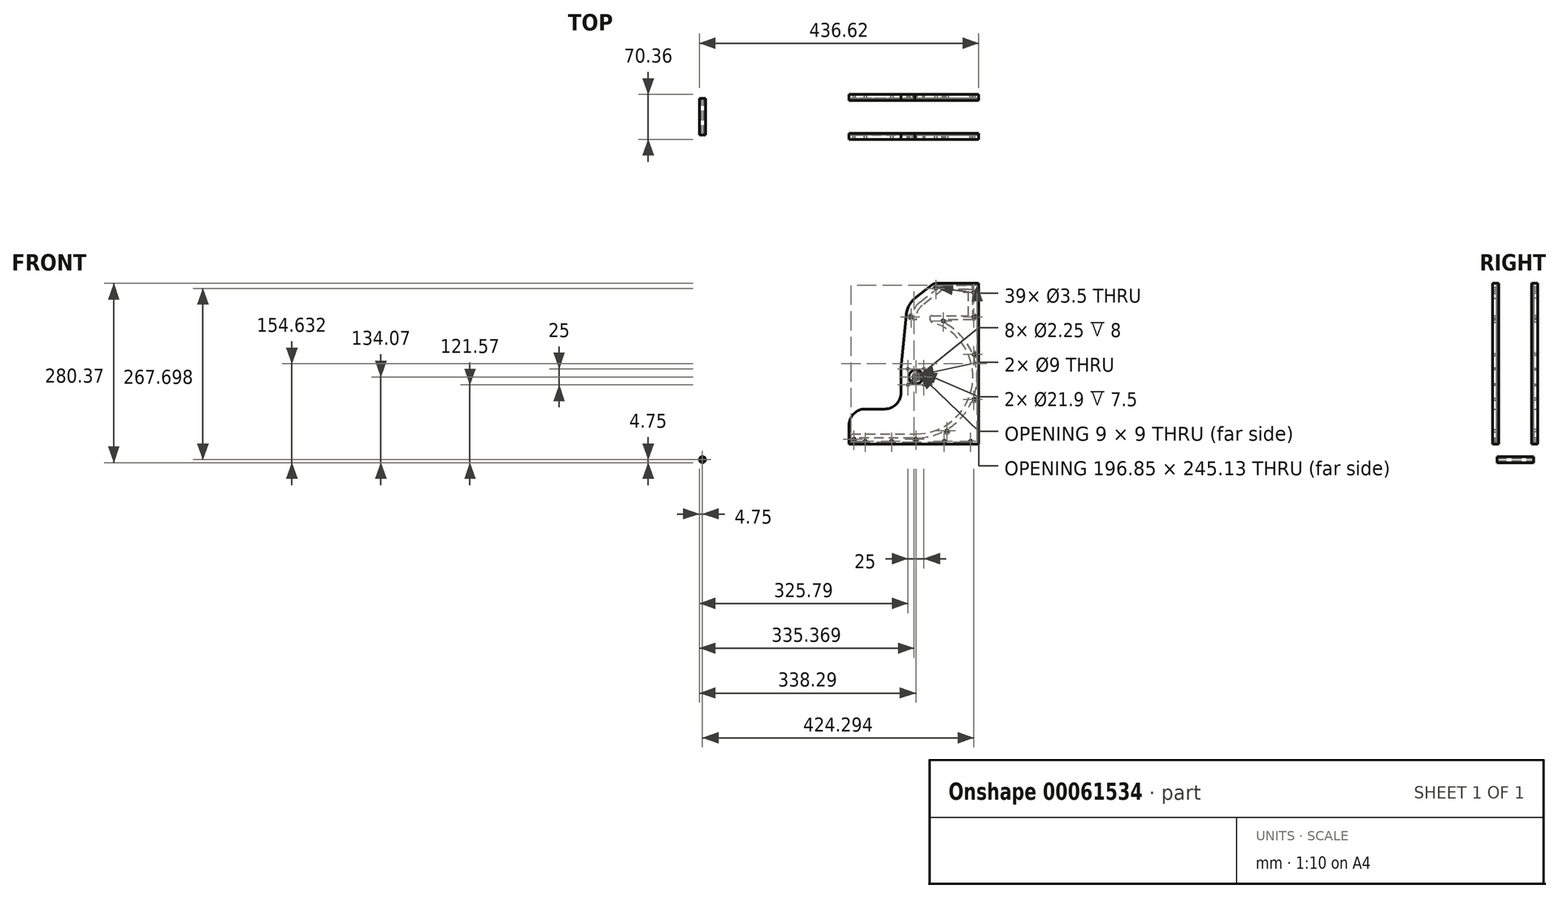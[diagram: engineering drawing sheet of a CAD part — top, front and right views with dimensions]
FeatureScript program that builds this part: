
annotation { "Feature Type Name" : "Feature", "Feature Type Description" : "" }
export const myFeature = defineFeature(function(context is Context, id is Id, definition is map)
    precondition{}
    {
        {
            var Q0;
            Q0=qCreatedBy(makeId("Front.planeOp"),FACE);
            var sketch = newSketch(context, id + "F0", { "sketchPlane" : qUnion([Q0])});
            skArc(sketch, "E0", {"start": v(0, -89.15) * mm, "mid": v(88.25, -12.66) * mm, "end": v(25.06, 85.56) * mm});
            skArc(sketch, "E1", {"start": v(4.37, -95.4) * mm, "mid": v(24.68, -92.26) * mm, "end": v(43.84, -84.85) * mm});
            skLineSegment(sketch, "E2.bottom", {"start": v(0, -89.15) * mm, "end": v(-101.35, -89.15) * mm});
            skLineSegment(sketch, "E2.top", {"start": v(-4.42, -95.5) * mm, "end": v(-92.18, -95.5) * mm});
            skLineSegment(sketch, "E2.right", {"start": v(-101.35, -89.15) * mm, "end": v(-101.35, -95.5) * mm});
            skLineSegment(sketch, "E3.bottom", {"start": v(82.3, 95.5) * mm, "end": v(24.82, 95.5) * mm});
            skLineSegment(sketch, "E4", {"start": v(22.07, 90.74) * mm, "end": v(25.06, 85.56) * mm});
            skLineSegment(sketch, "E5", {"start": v(95.5, -138.78) * mm, "end": v(95.5, 0) * mm, "construction": true});
            skCircle(sketch, "E6", {"center": v(42.65, 87.4) * mm, "radius": 1.75 * mm});
            skCircle(sketch, "E7", {"center": v(90.75, 34.96) * mm, "radius": 1.75 * mm});
            skArc(sketch, "E8", {"start": v(90.6, 30.21) * mm, "mid": v(95.19, 36.67) * mm, "end": v(87.45, 38.38) * mm});
            skCircle(sketch, "E9", {"center": v(90.75, -34.96) * mm, "radius": 1.75 * mm});
            skArc(sketch, "E10", {"start": v(87.45, -38.38) * mm, "mid": v(95.19, -36.67) * mm, "end": v(90.6, -30.21) * mm});
            skCircle(sketch, "E11", {"center": v(48.56, -84.27) * mm, "radius": 1.75 * mm});
            skArc(sketch, "E12", {"start": v(43.84, -84.85) * mm, "mid": v(50.93, -88.38) * mm, "end": v(51.42, -80.48) * mm});
            skCircle(sketch, "E13", {"center": v(-333.54, -129.32) * mm, "radius": 1.75 * mm});
            skCircle(sketch, "E14", {"center": v(-333.54, -129.32) * mm, "radius": 4.75 * mm});
            skCircle(sketch, "E15", {"center": v(-96.6, -97.25) * mm, "radius": 1.75 * mm});
            skArc(sketch, "E16", {"start": v(-101.01, -95.5) * mm, "mid": v(-96.6, -102) * mm, "end": v(-92.18, -95.5) * mm});
            skCircle(sketch, "E17", {"center": v(0, -97.25) * mm, "radius": 1.75 * mm});
            skArc(sketch, "E18", {"start": v(-4.42, -95.5) * mm, "mid": v(0.05, -102) * mm, "end": v(4.37, -95.4) * mm});
            skLineSegment(sketch, "E19.trimOffspring", {"start": v(-101.01, -95.5) * mm, "end": v(-101.35, -95.5) * mm});
            skArc(sketch, "E20.trimOffspring", {"start": v(51.42, -80.48) * mm, "mid": v(72.56, -62.1) * mm, "end": v(87.45, -38.38) * mm});
            skArc(sketch, "E21.trimOffspring", {"start": v(90.6, -30.21) * mm, "mid": v(95.5, 0) * mm, "end": v(90.6, 30.21) * mm});
            skArc(sketch, "E22.trimOffspring", {"start": v(87.45, 38.38) * mm, "mid": v(70.38, 64.56) * mm, "end": v(45.77, 83.82) * mm});
            skArc(sketch, "E23.trimOffspring", {"start": v(45.77, 83.82) * mm, "mid": v(47.26, 86.28) * mm, "end": v(47.06, 89.15) * mm});
            skLineSegment(sketch, "E24.trimOffspring", {"start": v(88.66, 89.15) * mm, "end": v(47.06, 89.15) * mm});
            skCircle(sketch, "E25", {"center": v(90.4, 93.9) * mm, "radius": 1.75 * mm});
            skArc(sketch, "E26", {"start": v(88.66, 89.49) * mm, "mid": v(95.16, 93.9) * mm, "end": v(88.66, 98.32) * mm});
            skLineSegment(sketch, "E27", {"start": v(88.66, 136.78) * mm, "end": v(88.66, 136.44) * mm});
            skLineSegment(sketch, "E28", {"start": v(82.3, 136.78) * mm, "end": v(82.3, 95.5) * mm});
            skLineSegment(sketch, "E29", {"start": v(82.3, 136.78) * mm, "end": v(88.66, 136.78) * mm});
            skLineSegment(sketch, "E30.trimOffspring", {"start": v(88.66, 89.49) * mm, "end": v(88.66, 89.15) * mm});
            skCircle(sketch, "E31", {"center": v(90.4, 132.03) * mm, "radius": 1.75 * mm});
            skArc(sketch, "E32", {"start": v(88.66, 127.61) * mm, "mid": v(95.16, 132.03) * mm, "end": v(88.66, 136.44) * mm});
            skLineSegment(sketch, "E33.trimOffspring", {"start": v(88.66, 127.61) * mm, "end": v(88.66, 98.32) * mm});
            skPoint(sketch, "E34.visualSharp", {"position": v(19.32, 95.5) * mm});
            skArc(sketch, "E34.filletArc", {"start": v(24.82, 95.5) * mm, "mid": v(22.07, 93.92) * mm, "end": v(22.07, 90.74) * mm});
            skSolve(sketch);
        }
        {
            var Q0;
            Q0=qSketchRegion(id+"F0",true);
            extrude(context, id + "F1", {"entities" : qUnion([Q0]), "depth" : 57.15 * mm});
        }
        {
            var Q0;
            Q0=qCreatedBy(makeId("Front.planeOp"),FACE);
            var sketch = newSketch(context, id + "F2", { "sketchPlane" : qUnion([Q0])});
            skArc(sketch, "E35", {"start": v(0.64, 89.15) * mm, "mid": v(-2.36, 89.12) * mm, "end": v(-5.35, 89) * mm});
            skLineSegment(sketch, "E36", {"start": v(0, 0) * mm, "end": v(0, 123.17) * mm, "construction": true});
            skLineSegment(sketch, "E37", {"start": v(119.91, 115.4) * mm, "end": v(119.91, 121.76) * mm});
            skLineSegment(sketch, "E38.0", {"start": v(82.3, 95.5) * mm, "end": v(24.82, 95.5) * mm, "construction": true});
            skArc(sketch, "E39.0", {"start": v(24.82, 95.5) * mm, "mid": v(22.07, 93.92) * mm, "end": v(22.07, 90.74) * mm, "construction": true});
            skArc(sketch, "E40", {"start": v(9.89, 111.61) * mm, "mid": v(2.27, 101.61) * mm, "end": v(0.64, 89.15) * mm});
            skCircle(sketch, "E41", {"center": v(-7.26, 93.62) * mm, "radius": 1.75 * mm});
            skArc(sketch, "E42", {"start": v(-5.15, 97.88) * mm, "mid": v(-12.01, 93.75) * mm, "end": v(-5.38, 89.26) * mm});
            skArc(sketch, "E43.trimOffspring", {"start": v(6.19, 116.77) * mm, "mid": v(-1.26, 108.4) * mm, "end": v(-5.15, 97.88) * mm});
            skArc(sketch, "E44.trimOffspring", {"start": v(-5.38, 89.26) * mm, "mid": v(-5.34, 88.91) * mm, "end": v(-5.3, 88.57) * mm});
            skLineSegment(sketch, "E45", {"start": v(88.66, 136.78) * mm, "end": v(88.66, 143.13) * mm});
            skLineSegment(sketch, "E46", {"start": v(88.66, 143.13) * mm, "end": v(40.23, 143.13) * mm});
            skPoint(sketch, "E47.0.start.orphan", {"position": v(82.3, 136.78) * mm});
            skLineSegment(sketch, "E48", {"start": v(88.66, 136.78) * mm, "end": v(42.4, 136.78) * mm});
            skLineSegment(sketch, "E49", {"start": v(6.19, 116.77) * mm, "end": v(28.82, 134.3) * mm});
            skLineSegment(sketch, "E50.0", {"start": v(9.89, 111.61) * mm, "end": v(42.4, 136.78) * mm});
            skPoint(sketch, "E51.orphan", {"position": v(32.03, 136.78) * mm});
            skPoint(sketch, "E52.orphan", {"position": v(-24.6, 136.78) * mm});
            skCircle(sketch, "E53", {"center": v(31.24, 138.38) * mm, "radius": 1.75 * mm});
            skArc(sketch, "E54", {"start": v(35.8, 139.7) * mm, "mid": v(28.33, 142.14) * mm, "end": v(28.82, 134.3) * mm});
            skLineSegment(sketch, "E55.trimOffspring", {"start": v(35.8, 139.7) * mm, "end": v(40.23, 143.13) * mm});
            skLineSegment(sketch, "E56.trimOffspring", {"start": v(32.03, 136.78) * mm, "end": v(32.3, 137) * mm});
            skSolve(sketch);
        }
        {
            var Q0;
            Q0=qSketchRegion(id+"F2",true);
            var Q1;
            Q1=makeQuery(id+"F1.opExtrude","CAP_FACE",FACE,{"disambiguationData":[OSD([sQuery(id+"F0.wireOp",EDGE,"E0"),sQuery(id+"F0.wireOp",EDGE,"E1"),sQuery(id+"F0.wireOp",EDGE,"E2.bottom"),sQuery(id+"F0.wireOp",EDGE,"E2.top"),sQuery(id+"F0.wireOp",EDGE,"E2.right"),sQuery(id+"F0.wireOp",EDGE,"E3.bottom"),sQuery(id+"F0.wireOp",EDGE,"E4"),sQuery(id+"F0.wireOp",EDGE,"E6"),sQuery(id+"F0.wireOp",EDGE,"E7"),sQuery(id+"F0.wireOp",EDGE,"E8"),sQuery(id+"F0.wireOp",EDGE,"E9"),sQuery(id+"F0.wireOp",EDGE,"E10"),sQuery(id+"F0.wireOp",EDGE,"E11"),sQuery(id+"F0.wireOp",EDGE,"E12"),sQuery(id+"F0.wireOp",EDGE,"E15"),sQuery(id+"F0.wireOp",EDGE,"E16"),sQuery(id+"F0.wireOp",EDGE,"E17"),sQuery(id+"F0.wireOp",EDGE,"E18"),sQuery(id+"F0.wireOp",EDGE,"E19.trimOffspring"),sQuery(id+"F0.wireOp",EDGE,"E20.trimOffspring"),sQuery(id+"F0.wireOp",EDGE,"E21.trimOffspring"),sQuery(id+"F0.wireOp",EDGE,"E22.trimOffspring"),sQuery(id+"F0.wireOp",EDGE,"E23.trimOffspring"),sQuery(id+"F0.wireOp",EDGE,"E24.trimOffspring"),sQuery(id+"F0.wireOp",EDGE,"E25"),sQuery(id+"F0.wireOp",EDGE,"E26"),sQuery(id+"F0.wireOp",EDGE,"E27"),sQuery(id+"F0.wireOp",EDGE,"E28"),sQuery(id+"F0.wireOp",EDGE,"E29"),sQuery(id+"F0.wireOp",EDGE,"E30.trimOffspring"),sQuery(id+"F0.wireOp",EDGE,"E31"),sQuery(id+"F0.wireOp",EDGE,"E32"),sQuery(id+"F0.wireOp",EDGE,"E33.trimOffspring"),sQuery(id+"F0.wireOp",EDGE,"E34.filletArc")])],"isStart":false});
            extrude(context, id + "F3", {"entities" : qUnion([Q0]), "endBound" : BoundingType.UP_TO_SURFACE, "endBoundEntityFace" : qUnion([Q1]), "depth" : 25.4 * mm});
        }
        {
            var Q0;
            Q0=qCreatedBy(makeId("Front.planeOp"),FACE);
            var sketch = newSketch(context, id + "F4", { "sketchPlane" : qUnion([Q0])});
            skLineSegment(sketch, "E57.bottom", {"start": v(98.33, 146.3) * mm, "end": v(-104.52, 146.3) * mm});
            skLineSegment(sketch, "E57.top", {"start": v(98.33, -105.18) * mm, "end": v(-104.52, -105.18) * mm});
            skLineSegment(sketch, "E57.left", {"start": v(98.33, 146.3) * mm, "end": v(98.33, -105.18) * mm});
            skLineSegment(sketch, "E57.right", {"start": v(-104.52, 146.3) * mm, "end": v(-104.52, -105.18) * mm});
            skSolve(sketch);
        }
        {
            var Q0;
            Q0=makeQuery(id+"F4.imprint","IMPRINT",FACE,{"disambiguationData":[TD([[makeQuery(id+"F4.imprint","IMPRINT",EDGE,{"derivedFrom":sQuery(id+"F4.wireOp",EDGE,"E57.bottom")}),1.0]])]});
            extrude(context, id + "F5", {"entities" : qUnion([Q0]), "depth" : 3.17 * mm, "hasSecondDirection" : true, "secondDirectionOppositeDirection" : true, "secondDirectionDepth" : 6.35 * mm});
        }
        {
            var Q0;
            Q0=makeQuery(id+"F5.opExtrude","CAP_FACE",FACE,{"disambiguationData":[OSD([sQuery(id+"F4.wireOp",EDGE,"E57.bottom"),sQuery(id+"F4.wireOp",EDGE,"E57.top"),sQuery(id+"F4.wireOp",EDGE,"E57.left"),sQuery(id+"F4.wireOp",EDGE,"E57.right")])],"isStart":true});
            var sketch = newSketch(context, id + "F6", { "sketchPlane" : qUnion([Q0])});
            skCircle(sketch, "E58", {"center": v(0, 0) * mm, "radius": 4.5 * mm});
            skSolve(sketch);
        }
        {
            var Q0;
            Q0 = qSketchRegion(id + "F6", true);
            extrude(context, id + "F7", {"entities" : qUnion([Q0]), "operationType" : NewBodyOperationType.REMOVE, "oppositeDirection" : true, "depth" : 25.4 * mm});
        }
        {
            var Q0;
            Q0=makeQuery(id+"F5.opExtrude","CAP_FACE",FACE,{"disambiguationData":[OSD([sQuery(id+"F4.wireOp",EDGE,"E57.bottom"),sQuery(id+"F4.wireOp",EDGE,"E57.top"),sQuery(id+"F4.wireOp",EDGE,"E57.left"),sQuery(id+"F4.wireOp",EDGE,"E57.right")])],"isStart":true});
            var sketch = newSketch(context, id + "F8", { "sketchPlane" : qUnion([Q0])});
            skCircle(sketch, "E59", {"center": v(0, 0) * mm, "radius": 10.95 * mm});
            skSolve(sketch);
        }
        {
            var Q0;
            Q0 = qSketchRegion(id + "F8", true);
            extrude(context, id + "F9", {"entities" : qUnion([Q0]), "operationType" : NewBodyOperationType.REMOVE, "oppositeDirection" : true, "depth" : 7.5 * mm});
        }
        {
            var Q0;
            Q0=makeQuery(id+"F5.opExtrude","CAP_FACE",FACE,{"disambiguationData":[OSD([sQuery(id+"F4.wireOp",EDGE,"E57.bottom"),sQuery(id+"F4.wireOp",EDGE,"E57.top"),sQuery(id+"F4.wireOp",EDGE,"E57.left"),sQuery(id+"F4.wireOp",EDGE,"E57.right")])],"isStart":true});
            var sketch = newSketch(context, id + "F10", { "sketchPlane" : qUnion([Q0])});
            skLineSegment(sketch, "E60.bottom", {"start": v(-12.5, 12.5) * mm, "end": v(12.5, 12.5) * mm, "construction": true});
            skLineSegment(sketch, "E60.top", {"start": v(-12.5, -12.5) * mm, "end": v(12.5, -12.5) * mm, "construction": true});
            skLineSegment(sketch, "E60.left", {"start": v(-12.5, 12.5) * mm, "end": v(-12.5, -12.5) * mm, "construction": true});
            skLineSegment(sketch, "E60.right", {"start": v(12.5, 12.5) * mm, "end": v(12.5, -12.5) * mm, "construction": true});
            skCircle(sketch, "E61", {"center": v(12.5, -12.5) * mm, "radius": 1.13 * mm});
            skCircle(sketch, "E62", {"center": v(-12.5, -12.5) * mm, "radius": 1.13 * mm});
            skCircle(sketch, "E63", {"center": v(-12.5, 12.5) * mm, "radius": 1.13 * mm});
            skCircle(sketch, "E64", {"center": v(12.5, 12.5) * mm, "radius": 1.13 * mm});
            skSolve(sketch);
        }
        {
            var Q0;
            Q0 = qSketchRegion(id + "F10", true);
            extrude(context, id + "F11", {"entities" : qUnion([Q0]), "operationType" : NewBodyOperationType.REMOVE, "oppositeDirection" : true, "depth" : 8 * mm});
        }
        {
            var Q0;
            Q0=makeQuery(id+"F5.opExtrude","CAP_FACE",FACE,{"disambiguationData":[OSD([sQuery(id+"F4.wireOp",EDGE,"E57.bottom"),sQuery(id+"F4.wireOp",EDGE,"E57.top"),sQuery(id+"F4.wireOp",EDGE,"E57.left"),sQuery(id+"F4.wireOp",EDGE,"E57.right")])],"isStart":false});
            var sketch = newSketch(context, id + "F12", { "sketchPlane" : qUnion([Q0])});
            skLineSegment(sketch, "E65", {"start": v(-23.15, 13) * mm, "end": v(-23.15, -24.84) * mm});
            skLineSegment(sketch, "E66", {"start": v(-148.38, -50.24) * mm, "end": v(-48.55, -50.24) * mm});
            skArc(sketch, "E67.0.0", {"start": v(-5.15, 97.88) * mm, "mid": v(-1.26, 108.4) * mm, "end": v(6.19, 116.77) * mm, "construction": true});
            skArc(sketch, "E67.0.2", {"start": v(6.19, 116.77) * mm, "mid": v(-1.26, 108.4) * mm, "end": v(-5.15, 97.88) * mm, "construction": true});
            skArc(sketch, "E68.0", {"start": v(-1.75, 122.87) * mm, "mid": v(-10.96, 111) * mm, "end": v(-15.16, 96.59) * mm});
            skCircle(sketch, "E69.0", {"center": v(-12.5, 12.5) * mm, "radius": 1.13 * mm, "construction": true});
            skArc(sketch, "E70.0", {"start": v(-23.1, 13.51) * mm, "mid": v(-23.14, 13) * mm, "end": v(-23.15, 12.5) * mm});
            skLineSegment(sketch, "E71", {"start": v(-15.16, 96.59) * mm, "end": v(-23.15, 13) * mm});
            skLineSegment(sketch, "E72.trimOffspring", {"start": v(-1.75, 122.87) * mm, "end": v(42.2, 156.9) * mm});
            skPoint(sketch, "E73.visualSharp", {"position": v(-23.15, -50.24) * mm});
            skArc(sketch, "E73.filletArc", {"start": v(-48.55, -50.24) * mm, "mid": v(-30.59, -42.8) * mm, "end": v(-23.15, -24.84) * mm});
            skLineSegment(sketch, "E74", {"start": v(42.2, 156.9) * mm, "end": v(-148.38, 156.9) * mm});
            skLineSegment(sketch, "E75", {"start": v(-148.38, -50.24) * mm, "end": v(-148.38, 156.9) * mm});
            skSolve(sketch);
        }
        {
            var Q0;
            Q0 = qSketchRegion(id + "F12", true);
            extrude(context, id + "F13", {"entities" : qUnion([Q0]), "operationType" : NewBodyOperationType.REMOVE, "oppositeDirection" : true, "depth" : 25.4 * mm});
        }
        {
            var Q0;
            Q0=makeQuery(id+"F13.boolean.opBoolean","INTERSECT",EDGE,{"derivedFrom":[makeQuery(id+"F5.opExtrude","SWEPT_FACE",FACE,{"disambiguationData":[OSD([sQuery(id+"F4.wireOp",EDGE,"E57.bottom")])]}),makeQuery(id+"F13.opExtrude","SWEPT_FACE",FACE,{"disambiguationData":[OSD([sQuery(id+"F12.wireOp",EDGE,"E72.trimOffspring")])]})]});
            fillet(context, id + "F14", {"entities" : qUnion([Q0]), "radius" : 12.7 * mm, "tangentPropagation" : true, "allowEdgeOverflow" : false});
        }
        {
            var Q0;
            Q0=makeQuery(id+"F13.boolean.opBoolean","INTERSECT",EDGE,{"derivedFrom":[makeQuery(id+"F5.opExtrude","SWEPT_FACE",FACE,{"disambiguationData":[OSD([sQuery(id+"F4.wireOp",EDGE,"E57.right")])]}),makeQuery(id+"F13.opExtrude","SWEPT_FACE",FACE,{"disambiguationData":[OSD([sQuery(id+"F12.wireOp",EDGE,"E66")])]})]});
            fillet(context, id + "F15", {"entities" : qUnion([Q0]), "radius" : 25.4 * mm, "tangentPropagation" : true, "allowEdgeOverflow" : false});
        }
        {
            var Q0;
            Q0=makeQuery(id+"F5.opExtrude","CAP_FACE",FACE,{"disambiguationData":[OSD([sQuery(id+"F4.wireOp",EDGE,"E57.bottom"),sQuery(id+"F4.wireOp",EDGE,"E57.top"),sQuery(id+"F4.wireOp",EDGE,"E57.left"),sQuery(id+"F4.wireOp",EDGE,"E57.right")])],"isStart":false});
            var sketch = newSketch(context, id + "F16", { "sketchPlane" : qUnion([Q0])});
            skCircle(sketch, "E76.0", {"center": v(-96.6, -97.25) * mm, "radius": 1.75 * mm});
            skCircle(sketch, "E77.0", {"center": v(0, -97.25) * mm, "radius": 1.75 * mm});
            skCircle(sketch, "E78.0", {"center": v(48.56, -84.27) * mm, "radius": 1.75 * mm});
            skCircle(sketch, "E79.0", {"center": v(90.75, -34.96) * mm, "radius": 1.75 * mm});
            skCircle(sketch, "E80.0", {"center": v(90.75, 34.96) * mm, "radius": 1.75 * mm});
            skCircle(sketch, "E81.0", {"center": v(42.65, 87.4) * mm, "radius": 1.75 * mm});
            skCircle(sketch, "E82.0", {"center": v(90.4, 93.9) * mm, "radius": 1.75 * mm});
            skCircle(sketch, "E83.0", {"center": v(90.4, 132.03) * mm, "radius": 1.75 * mm});
            skCircle(sketch, "E84.0", {"center": v(31.24, 138.38) * mm, "radius": 1.75 * mm});
            skCircle(sketch, "E85.0", {"center": v(-7.26, 93.62) * mm, "radius": 1.75 * mm});
            skSolve(sketch);
        }
        {
            var Q0;
            Q0 = qSketchRegion(id + "F16", true);
            extrude(context, id + "F17", {"entities" : qUnion([Q0]), "operationType" : NewBodyOperationType.REMOVE, "oppositeDirection" : true, "depth" : 25.4 * mm});
        }
        {
            var Q0;
            Q0=makeQuery(id+"F5.opExtrude","CAP_FACE",FACE,{"disambiguationData":[OSD([sQuery(id+"F4.wireOp",EDGE,"E57.bottom"),sQuery(id+"F4.wireOp",EDGE,"E57.top"),sQuery(id+"F4.wireOp",EDGE,"E57.left"),sQuery(id+"F4.wireOp",EDGE,"E57.right")])],"isStart":false});
            var sketch = newSketch(context, id + "F18", { "sketchPlane" : qUnion([Q0])});
            skArc(sketch, "E86.0.0", {"start": v(25.06, 85.56) * mm, "mid": v(88.25, -12.66) * mm, "end": v(0, -89.15) * mm});
            skLineSegment(sketch, "E86.0.1", {"start": v(0, -89.15) * mm, "end": v(-101.35, -89.15) * mm});
            skLineSegment(sketch, "E86.0.2", {"start": v(-101.35, -89.15) * mm, "end": v(-101.35, -95.5) * mm});
            skLineSegment(sketch, "E86.0.3", {"start": v(-101.35, -95.5) * mm, "end": v(-101.01, -95.5) * mm});
            skArc(sketch, "E86.0.4", {"start": v(-101.01, -95.5) * mm, "mid": v(-96.6, -102) * mm, "end": v(-92.18, -95.5) * mm});
            skLineSegment(sketch, "E86.0.5", {"start": v(-92.18, -95.5) * mm, "end": v(-4.42, -95.5) * mm});
            skArc(sketch, "E86.0.6", {"start": v(-4.42, -95.5) * mm, "mid": v(0.05, -102) * mm, "end": v(4.37, -95.4) * mm});
            skArc(sketch, "E86.0.7", {"start": v(4.37, -95.4) * mm, "mid": v(24.68, -92.26) * mm, "end": v(43.84, -84.85) * mm});
            skArc(sketch, "E86.0.8", {"start": v(43.84, -84.85) * mm, "mid": v(50.93, -88.38) * mm, "end": v(51.42, -80.48) * mm});
            skArc(sketch, "E86.0.9", {"start": v(51.42, -80.48) * mm, "mid": v(72.56, -62.1) * mm, "end": v(87.45, -38.38) * mm});
            skArc(sketch, "E86.0.10", {"start": v(87.45, -38.38) * mm, "mid": v(95.19, -36.67) * mm, "end": v(90.6, -30.21) * mm});
            skArc(sketch, "E86.0.11", {"start": v(90.6, -30.21) * mm, "mid": v(95.5, 0) * mm, "end": v(90.6, 30.21) * mm});
            skArc(sketch, "E86.0.12", {"start": v(90.6, 30.21) * mm, "mid": v(95.19, 36.67) * mm, "end": v(87.45, 38.38) * mm});
            skArc(sketch, "E86.0.13", {"start": v(87.45, 38.38) * mm, "mid": v(70.38, 64.56) * mm, "end": v(45.77, 83.82) * mm});
            skArc(sketch, "E86.0.14", {"start": v(45.77, 83.82) * mm, "mid": v(47.26, 86.28) * mm, "end": v(47.06, 89.15) * mm});
            skLineSegment(sketch, "E86.0.15", {"start": v(47.06, 89.15) * mm, "end": v(88.66, 89.15) * mm});
            skLineSegment(sketch, "E86.0.16", {"start": v(88.66, 89.15) * mm, "end": v(88.66, 89.49) * mm});
            skArc(sketch, "E86.0.17", {"start": v(88.66, 89.49) * mm, "mid": v(95.16, 93.9) * mm, "end": v(88.66, 98.32) * mm});
            skLineSegment(sketch, "E86.0.18", {"start": v(88.66, 98.32) * mm, "end": v(88.66, 127.61) * mm});
            skArc(sketch, "E86.0.19", {"start": v(88.66, 127.61) * mm, "mid": v(95.16, 132.03) * mm, "end": v(88.66, 136.44) * mm});
            skLineSegment(sketch, "E86.0.20", {"start": v(88.66, 136.44) * mm, "end": v(88.66, 136.78) * mm});
            skLineSegment(sketch, "E86.0.21", {"start": v(88.66, 136.78) * mm, "end": v(82.3, 136.78) * mm});
            skLineSegment(sketch, "E86.0.22", {"start": v(82.3, 136.78) * mm, "end": v(82.3, 95.5) * mm});
            skLineSegment(sketch, "E86.0.23", {"start": v(82.3, 95.5) * mm, "end": v(24.82, 95.5) * mm});
            skArc(sketch, "E86.0.24", {"start": v(24.82, 95.5) * mm, "mid": v(22.07, 93.92) * mm, "end": v(22.07, 90.74) * mm});
            skLineSegment(sketch, "E86.0.25", {"start": v(22.07, 90.74) * mm, "end": v(25.06, 85.56) * mm});
            skArc(sketch, "E87.0.0", {"start": v(-5.35, 89) * mm, "mid": v(-2.36, 89.12) * mm, "end": v(0.64, 89.15) * mm});
            skArc(sketch, "E87.0.1", {"start": v(0.64, 89.15) * mm, "mid": v(2.27, 101.61) * mm, "end": v(9.89, 111.61) * mm});
            skLineSegment(sketch, "E87.0.2", {"start": v(9.89, 111.61) * mm, "end": v(42.4, 136.78) * mm});
            skLineSegment(sketch, "E87.0.3", {"start": v(42.4, 136.78) * mm, "end": v(88.66, 136.78) * mm});
            skLineSegment(sketch, "E87.0.4", {"start": v(88.66, 136.78) * mm, "end": v(88.66, 143.13) * mm});
            skLineSegment(sketch, "E87.0.5", {"start": v(88.66, 143.13) * mm, "end": v(40.23, 143.13) * mm});
            skLineSegment(sketch, "E87.0.6", {"start": v(40.23, 143.13) * mm, "end": v(35.8, 139.7) * mm});
            skArc(sketch, "E87.0.7", {"start": v(35.8, 139.7) * mm, "mid": v(28.33, 142.14) * mm, "end": v(28.82, 134.3) * mm});
            skLineSegment(sketch, "E87.0.8", {"start": v(28.82, 134.3) * mm, "end": v(6.19, 116.77) * mm});
            skArc(sketch, "E87.0.9", {"start": v(6.19, 116.77) * mm, "mid": v(-1.26, 108.4) * mm, "end": v(-5.15, 97.88) * mm});
            skArc(sketch, "E87.0.10", {"start": v(-5.15, 97.88) * mm, "mid": v(-12.01, 93.75) * mm, "end": v(-5.38, 89.26) * mm});
            skArc(sketch, "E87.0.11", {"start": v(-5.38, 89.26) * mm, "mid": v(-5.37, 89.13) * mm, "end": v(-5.35, 89) * mm});
            skSolve(sketch);
        }
        {
            var Q0;
            Q0 = qSketchRegion(id + "F18", true);
            extrude(context, id + "F19", {"entities" : qUnion([Q0]), "operationType" : NewBodyOperationType.REMOVE, "depth" : 63.5 * mm, "hasSecondDirection" : true, "secondDirectionOppositeDirection" : true, "secondDirectionDepth" : 2.92 * mm});
        }
        {
            var Q0;
            Q0=makeQuery(id+"F5.opExtrude","CAP_FACE",FACE,{"disambiguationData":[OSD([sQuery(id+"F4.wireOp",EDGE,"E57.bottom"),sQuery(id+"F4.wireOp",EDGE,"E57.top"),sQuery(id+"F4.wireOp",EDGE,"E57.left"),sQuery(id+"F4.wireOp",EDGE,"E57.right")])],"isStart":false});
            cPlane(context, id + "F20", {"entities" : qUnion([Q0]), "cplaneType" : CPlaneType.OFFSET, "offset" : 25.65 * mm, "width" : 152.4 * mm, "height" : 152.4 * mm});
        }
        {
            var Q0;
            Q0=makeQuery(id+"F5.opExtrude","SWEPT_BODY",BODY,{"disambiguationData":[OSD([sQuery(id+"F4.wireOp",EDGE,"E57.bottom"),sQuery(id+"F4.wireOp",EDGE,"E57.top"),sQuery(id+"F4.wireOp",EDGE,"E57.left"),sQuery(id+"F4.wireOp",EDGE,"E57.right")])]});
            var Q1;
            Q1=qCreatedBy(id+"F20.planeOp",FACE);
            mirror(context, id + "F21", {"entities" : qUnion([Q0]), "mirrorPlane" : qUnion([Q1])});
        }
        {
            var Q0;
            Q0=makeQuery(id+"F21.opPattern","COPY",FACE,{"derivedFrom":makeQuery(id+"F5.opExtrude","CAP_FACE",FACE,{"disambiguationData":[OSD([sQuery(id+"F4.wireOp",EDGE,"E57.bottom"),sQuery(id+"F4.wireOp",EDGE,"E57.top"),sQuery(id+"F4.wireOp",EDGE,"E57.left"),sQuery(id+"F4.wireOp",EDGE,"E57.right")])],"isStart":true}),"instanceName":"1"});
            var sketch = newSketch(context, id + "F22", { "sketchPlane" : qUnion([Q0])});
            skCircle(sketch, "E88", {"center": v(85.63, -100.42) * mm, "radius": 1.75 * mm});
            skCircle(sketch, "E89", {"center": v(44.36, -100.42) * mm, "radius": 1.75 * mm});
            skCircle(sketch, "E90", {"center": v(-79.12, -100.42) * mm, "radius": 1.75 * mm});
            skCircle(sketch, "E91", {"center": v(-37.85, -100.42) * mm, "radius": 1.75 * mm});
            skSolve(sketch);
        }
        {
            var Q0;
            Q0 = qSketchRegion(id + "F22", true);
            extrude(context, id + "F23", {"entities" : qUnion([Q0]), "operationType" : NewBodyOperationType.REMOVE, "endBound" : BoundingType.THROUGH_ALL, "oppositeDirection" : true, "depth" : 25.4 * mm});
        }
        {
            var Q0;
            Q0=makeQuery(id+"F5.opExtrude","CAP_FACE",FACE,{"disambiguationData":[OSD([sQuery(id+"F4.wireOp",EDGE,"E57.bottom"),sQuery(id+"F4.wireOp",EDGE,"E57.top"),sQuery(id+"F4.wireOp",EDGE,"E57.left"),sQuery(id+"F4.wireOp",EDGE,"E57.right")])],"isStart":false});
            var sketch = newSketch(context, id + "F24", { "sketchPlane" : qUnion([Q0])});
            skCircle(sketch, "E92.0", {"center": v(-79.12, -100.42) * mm, "radius": 1.75 * mm});
            skCircle(sketch, "E93.0", {"center": v(-37.85, -100.42) * mm, "radius": 1.75 * mm});
            skCircle(sketch, "E94.0", {"center": v(44.36, -100.42) * mm, "radius": 1.75 * mm});
            skCircle(sketch, "E95.0", {"center": v(85.63, -100.42) * mm, "radius": 1.75 * mm});
            skSolve(sketch);
        }
        {
            var Q0;
            Q0 = qSketchRegion(id + "F24", true);
            extrude(context, id + "F25", {"entities" : qUnion([Q0]), "operationType" : NewBodyOperationType.REMOVE, "oppositeDirection" : true, "depth" : 25.4 * mm});
        }
    });
